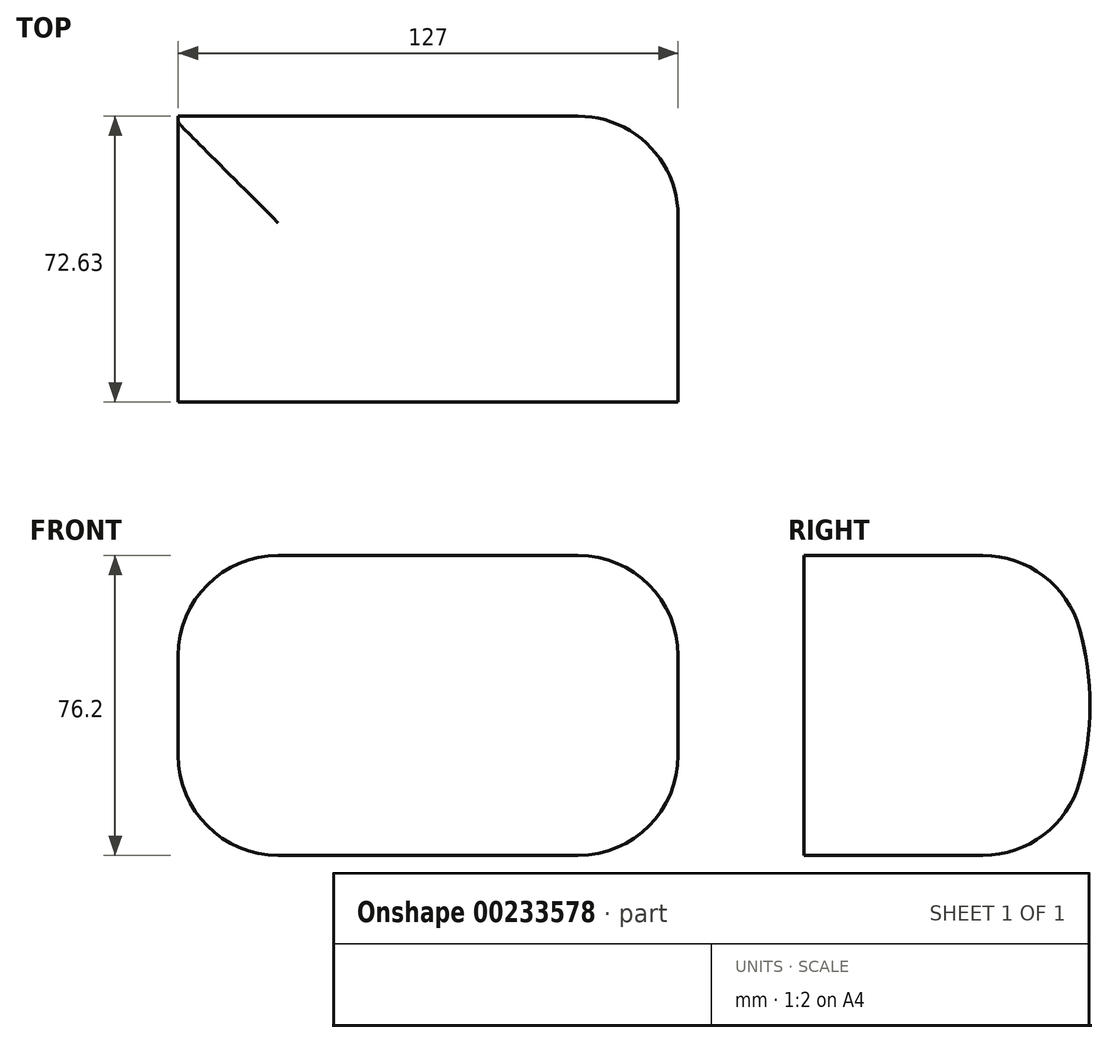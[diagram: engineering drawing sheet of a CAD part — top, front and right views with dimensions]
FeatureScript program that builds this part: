
annotation { "Feature Type Name" : "Feature", "Feature Type Description" : "" }
export const myFeature = defineFeature(function(context is Context, id is Id, definition is map)
    precondition{}
    {
        {
            var Q0;
            Q0=qCreatedBy(makeId("Front.planeOp"),FACE);
            var sketch = newSketch(context, id + "F0", { "sketchPlane" : qUnion([Q0])});
            skLineSegment(sketch, "E0.bottom", {"start": v(63.5, -38.1) * mm, "end": v(-63.5, -38.1) * mm});
            skLineSegment(sketch, "E0.top", {"start": v(63.5, 38.1) * mm, "end": v(-63.5, 38.1) * mm});
            skLineSegment(sketch, "E0.left", {"start": v(63.5, -38.1) * mm, "end": v(63.5, 38.1) * mm});
            skLineSegment(sketch, "E0.right", {"start": v(-63.5, -38.1) * mm, "end": v(-63.5, 38.1) * mm});
            skPoint(sketch, "E0.middle", {"position": v(0, 0) * mm});
            skSolve(sketch);
        }
        {
            var Q0;
            Q0=makeQuery(id+"F0.imprint","IMPRINT",FACE,{"disambiguationData":[TD([[makeQuery(id+"F0.imprint","IMPRINT",EDGE,{"derivedFrom":sQuery(id+"F0.wireOp",EDGE,"E0.bottom")}),-1.0]])]});
            extrude(context, id + "F1", {"entities" : qUnion([Q0]), "depth" : 76.2 * mm});
        }
        {
            var Q0;
            Q0=makeQuery(id+"F1.opExtrude","SWEPT_FACE",FACE,{"disambiguationData":[OSD([sQuery(id+"F0.wireOp",EDGE,"E0.right")])]});
            var sketch = newSketch(context, id + "F2", { "sketchPlane" : qUnion([Q0])});
            skCircle(sketch, "E1", {"center": v(76.2, 0) * mm, "radius": 72.63 * mm});
            skLineSegment(sketch, "E2", {"start": v(68.95, 72.27) * mm, "end": v(-52.1, 60.12) * mm});
            skLineSegment(sketch, "E3", {"start": v(-52.1, 60.12) * mm, "end": v(-33.1, -48.53) * mm});
            skLineSegment(sketch, "E4", {"start": v(-33.1, -48.53) * mm, "end": v(71.98, -72.5) * mm});
            skSolve(sketch);
        }
        {
            var Q0;
            {var subQ6=sQuery(id+"F2.wireOp",EDGE,"E2");Q0=makeQuery(id+"F2.imprint","IMPRINT",FACE,{"disambiguationData":[TD([[makeQuery(id+"F2.imprint","IMPRINT",EDGE,{"derivedFrom":subQ6}),1.0]])]});}
            var Q1;
            {var subQ1=sQuery(id+"F0.wireOp",EDGE,"E0.right");var subQ6=makeQuery(id+"F1.opExtrude","CAP_EDGE",EDGE,{"disambiguationData":[OSD([subQ1])],"isStart":true});Q1=makeQuery(id+"F2.imprint","IMPRINT",FACE,{"disambiguationData":[TD([[makeQuery(id+"F2.imprint","IMPRINT",EDGE,{"derivedFrom":subQ6}),-1.0]])]});}
            extrude(context, id + "F3", {"entities" : qUnion([Q0, Q1]), "operationType" : NewBodyOperationType.REMOVE, "endBound" : BoundingType.THROUGH_ALL, "oppositeDirection" : true, "depth" : 25.4 * mm});
        }
        {
            var Q0;
            Q0=makeQuery(id+"F1.opExtrude","SWEPT_EDGE",EDGE,{"disambiguationData":[OSD([sQuery(id+"F0.wireOp",EDGE,"E0.top"),sQuery(id+"F0.wireOp",EDGE,"E0.right")])]});
            var Q1;
            Q1=makeQuery(id+"F1.opExtrude","SWEPT_EDGE",EDGE,{"disambiguationData":[OSD([sQuery(id+"F0.wireOp",EDGE,"E0.top"),sQuery(id+"F0.wireOp",EDGE,"E0.left")])]});
            var Q2;
            Q2=makeQuery(id+"F1.opExtrude","SWEPT_EDGE",EDGE,{"disambiguationData":[OSD([sQuery(id+"F0.wireOp",EDGE,"E0.bottom"),sQuery(id+"F0.wireOp",EDGE,"E0.right")])]});
            var Q3;
            Q3=makeQuery(id+"F1.opExtrude","SWEPT_EDGE",EDGE,{"disambiguationData":[OSD([sQuery(id+"F0.wireOp",EDGE,"E0.bottom"),sQuery(id+"F0.wireOp",EDGE,"E0.left")])]});
            var Q4;
            Q4=makeQuery(id+"F3.boolean.opBoolean","INTERSECT",EDGE,{"derivedFrom":[makeQuery(id+"F1.opExtrude","SWEPT_FACE",FACE,{"disambiguationData":[OSD([sQuery(id+"F0.wireOp",EDGE,"E0.left")])]}),makeQuery(id+"F3.opExtrude","SWEPT_FACE",FACE,{"disambiguationData":[OSD([sQuery(id+"F2.wireOp",EDGE,"E1")])]})]});
            var Q5;
            Q5=makeQuery(id+"F3.boolean.opBoolean","COPY",EDGE,{"derivedFrom":makeQuery(id+"F3.opExtrude","CAP_EDGE",EDGE,{"disambiguationData":[OSD([sQuery(id+"F2.wireOp",EDGE,"E1")])],"isStart":true})});
            var Q6;
            Q6=makeQuery(id+"F3.boolean.opBoolean","INTERSECT",EDGE,{"derivedFrom":[makeQuery(id+"F1.opExtrude","SWEPT_FACE",FACE,{"disambiguationData":[OSD([sQuery(id+"F0.wireOp",EDGE,"E0.bottom")])]}),makeQuery(id+"F3.opExtrude","SWEPT_FACE",FACE,{"disambiguationData":[OSD([sQuery(id+"F2.wireOp",EDGE,"E1")])]})]});
            var Q7;
            Q7=makeQuery(id+"F3.boolean.opBoolean","INTERSECT",EDGE,{"derivedFrom":[makeQuery(id+"F1.opExtrude","SWEPT_FACE",FACE,{"disambiguationData":[OSD([sQuery(id+"F0.wireOp",EDGE,"E0.top")])]}),makeQuery(id+"F3.opExtrude","SWEPT_FACE",FACE,{"disambiguationData":[OSD([sQuery(id+"F2.wireOp",EDGE,"E1")])]})]});
            fillet(context, id + "F4", {"entities" : qUnion([Q0, Q1, Q2, Q3, Q4, Q5, Q6, Q7]), "radius" : 25.4 * mm, "tangentPropagation" : true, "allowEdgeOverflow" : false});
        }
    });
